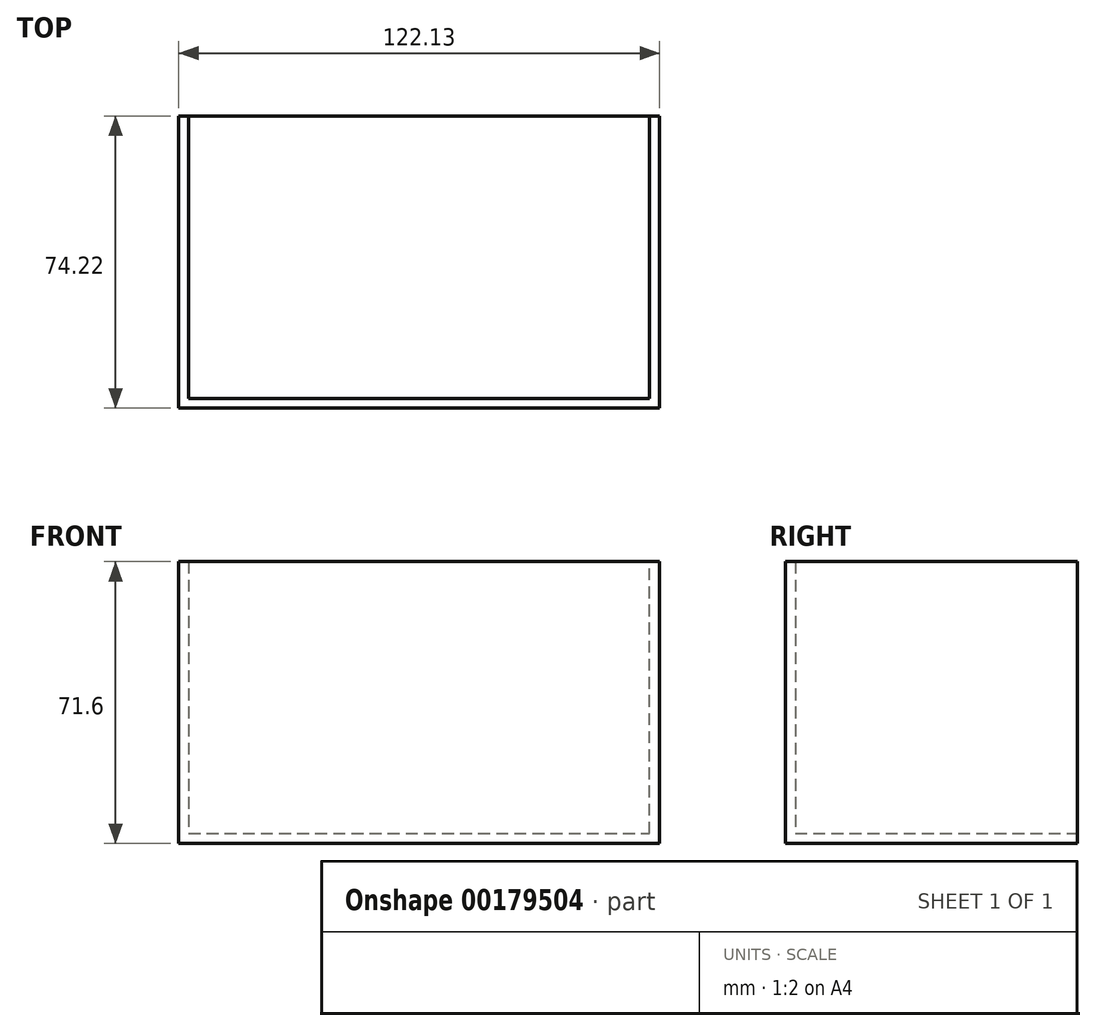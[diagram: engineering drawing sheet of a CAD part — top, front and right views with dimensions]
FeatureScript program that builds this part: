
annotation { "Feature Type Name" : "Feature", "Feature Type Description" : "" }
export const myFeature = defineFeature(function(context is Context, id is Id, definition is map)
    precondition{}
    {
        {
            var Q0;
            Q0=qCreatedBy(makeId("Top.planeOp"),FACE);
            var sketch = newSketch(context, id + "F0", { "sketchPlane" : qUnion([Q0])});
            skLineSegment(sketch, "E0.bottom", {"start": v(0, 0) * mm, "end": v(122.13, 0) * mm});
            skLineSegment(sketch, "E0.top", {"start": v(0, 74.22) * mm, "end": v(122.13, 74.22) * mm});
            skLineSegment(sketch, "E0.left", {"start": v(0, 0) * mm, "end": v(0, 74.22) * mm});
            skLineSegment(sketch, "E0.right", {"start": v(122.13, 0) * mm, "end": v(122.13, 74.22) * mm});
            skSolve(sketch);
        }
        {
            var Q0;
            Q0 = qSketchRegion(id + "F0", true);
            extrude(context, id + "F1", {"entities" : qUnion([Q0]), "depth" : 71.6 * mm});
        }
        {
            var Q0;
            Q0=makeQuery(id+"F1.opExtrude","CAP_FACE",FACE,{"disambiguationData":[OSD([sQuery(id+"F0.wireOp",EDGE,"E0.bottom"),sQuery(id+"F0.wireOp",EDGE,"E0.top"),sQuery(id+"F0.wireOp",EDGE,"E0.left"),sQuery(id+"F0.wireOp",EDGE,"E0.right")])],"isStart":false});
            shell(context, id + "F2", {"entities" : qUnion([Q0]), "thickness" : 2.5 * mm});
        }
        {
            var Q0;
            Q0=makeQuery(id+"F1.opExtrude","SWEPT_FACE",FACE,{"disambiguationData":[OSD([sQuery(id+"F0.wireOp",EDGE,"E0.top")])]});
            var sketch = newSketch(context, id + "F3", { "sketchPlane" : qUnion([Q0])});
            skLineSegment(sketch, "E1.0.0", {"start": v(-2.5, 2.5) * mm, "end": v(-119.63, 2.5) * mm});
            skLineSegment(sketch, "E1.0.1", {"start": v(-119.63, 2.5) * mm, "end": v(-119.63, 71.6) * mm});
            skLineSegment(sketch, "E1.0.2", {"start": v(-119.63, 71.6) * mm, "end": v(-2.5, 71.6) * mm});
            skLineSegment(sketch, "E1.0.3", {"start": v(-2.5, 71.6) * mm, "end": v(-2.5, 2.5) * mm});
            skSolve(sketch);
        }
        {
            var Q0;
            Q0=makeQuery(id+"F3.imprint","IMPRINT",FACE,{"disambiguationData":[TD([[makeQuery(id+"F3.imprint","IMPRINT",EDGE,{"derivedFrom":sQuery(id+"F3.wireOp",EDGE,"E1.0.0")}),-1.0]])]});
            extrude(context, id + "F4", {"entities" : qUnion([Q0]), "operationType" : NewBodyOperationType.REMOVE, "oppositeDirection" : true, "depth" : 25 * mm});
        }
    });
